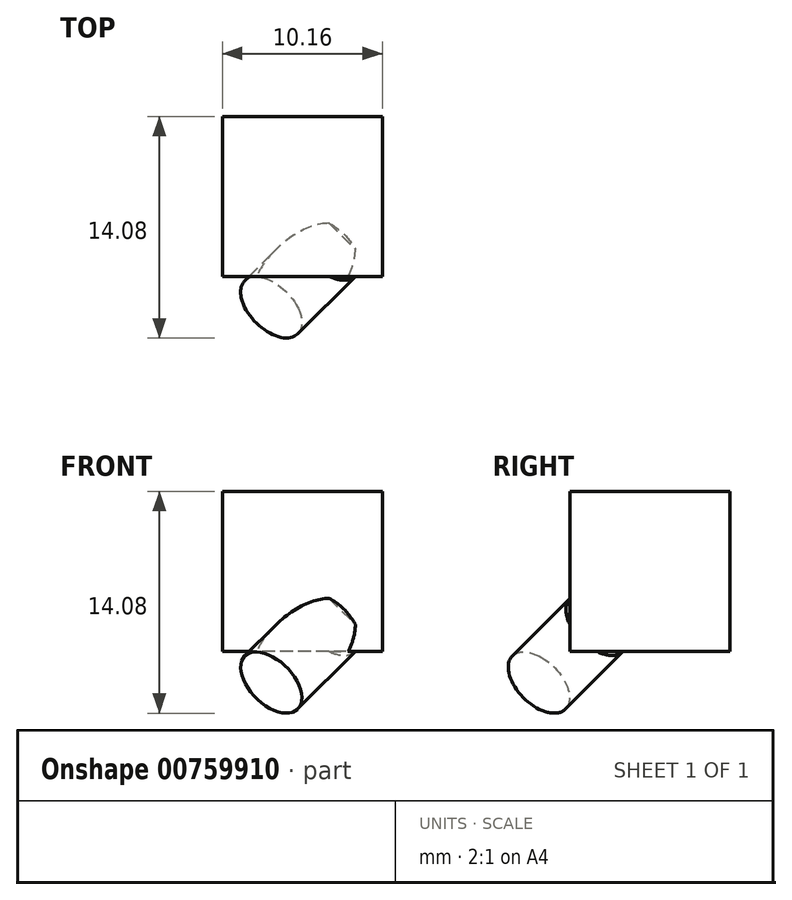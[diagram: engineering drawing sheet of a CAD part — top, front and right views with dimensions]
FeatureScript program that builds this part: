
annotation { "Feature Type Name" : "Feature", "Feature Type Description" : "" }
export const myFeature = defineFeature(function(context is Context, id is Id, definition is map)
    precondition{}
    {
        {
            var Q0;
            Q0=qCreatedBy(makeId("Top.planeOp"),FACE);
            var sketch = newSketch(context, id + "F0", { "sketchPlane" : qUnion([Q0])});
            skLineSegment(sketch, "E0.bottom", {"start": v(5.08, 5.08) * mm, "end": v(-5.08, 5.08) * mm});
            skLineSegment(sketch, "E0.top", {"start": v(5.08, -5.08) * mm, "end": v(-5.08, -5.08) * mm});
            skLineSegment(sketch, "E0.left", {"start": v(5.08, 5.08) * mm, "end": v(5.08, -5.08) * mm});
            skLineSegment(sketch, "E0.right", {"start": v(-5.08, 5.08) * mm, "end": v(-5.08, -5.08) * mm});
            skPoint(sketch, "E0.middle", {"position": v(0, 0) * mm});
            skSolve(sketch);
        }
        {
            var Q0;
            Q0 = qSketchRegion(id + "F0", true);
            extrude(context, id + "F1", {"entities" : qUnion([Q0]), "depth" : 10.16 * mm, "offsetDistance" : 25.4 * mm});
        }
        {
            var Q0;
            Q0=makeQuery(id+"F1.opExtrude","CAP_VERTEX",VERTEX,{"disambiguationData":[OSD([sQuery(id+"F0.wireOp",EDGE,"E0.top"),sQuery(id+"F0.wireOp",EDGE,"E0.right")])],"isStart":false});
            var Q1;
            Q1=makeQuery(id+"F1.opExtrude","CAP_VERTEX",VERTEX,{"disambiguationData":[OSD([sQuery(id+"F0.wireOp",EDGE,"E0.top"),sQuery(id+"F0.wireOp",EDGE,"E0.left")])],"isStart":true});
            var Q2;
            Q2=makeQuery(id+"F1.opExtrude","CAP_VERTEX",VERTEX,{"disambiguationData":[OSD([sQuery(id+"F0.wireOp",EDGE,"E0.bottom"),sQuery(id+"F0.wireOp",EDGE,"E0.right")])],"isStart":true});
            cPlane(context, id + "F2", {"entities" : qUnion([Q0, Q1, Q2]), "cplaneType" : CPlaneType.THREE_POINT, "offset" : 25.4 * mm, "width" : 152.4 * mm, "height" : 152.4 * mm});
        }
        {
            var Q0;
            Q0=qCreatedBy(id+"F2.planeOp",FACE);
            var sketch = newSketch(context, id + "F3", { "sketchPlane" : qUnion([Q0])});
            skCircle(sketch, "E1", {"center": v(2.07, 3.6) * mm, "radius": 2.38 * mm});
            skSolve(sketch);
        }
        {
            var Q0;
            Q0 = qSketchRegion(id + "F3", true);
            extrude(context, id + "F4", {"entities" : qUnion([Q0]), "operationType" : NewBodyOperationType.ADD, "depth" : 6.35 * mm, "offsetDistance" : 25.4 * mm});
        }
    });
